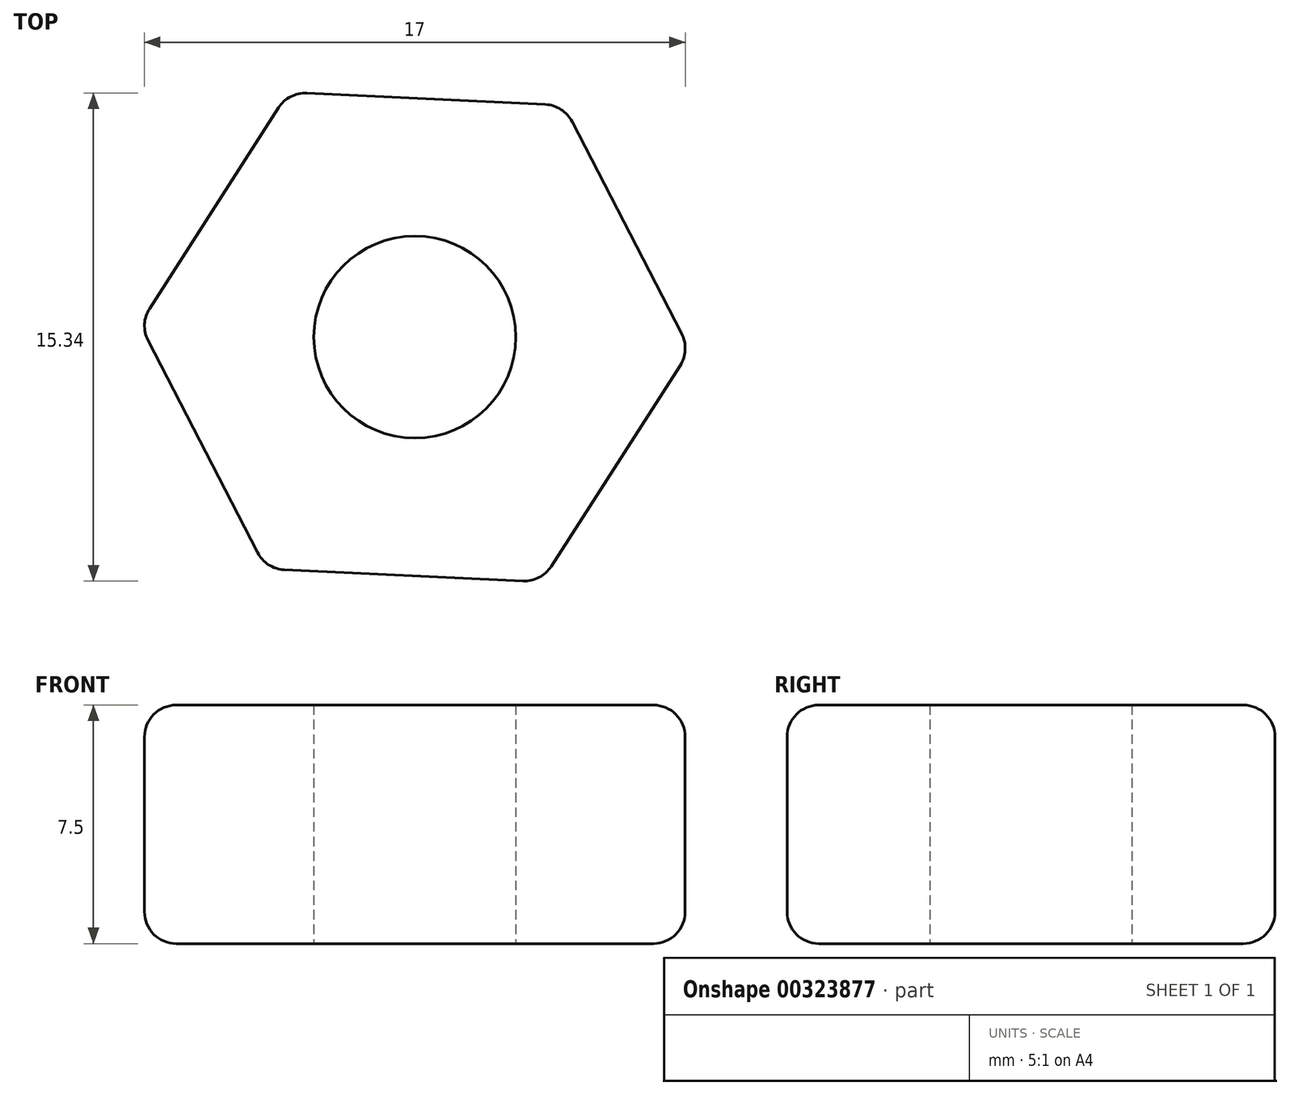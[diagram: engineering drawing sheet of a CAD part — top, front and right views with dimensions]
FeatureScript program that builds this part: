
annotation { "Feature Type Name" : "Feature", "Feature Type Description" : "" }
export const myFeature = defineFeature(function(context is Context, id is Id, definition is map)
    precondition{}
    {
        {
            var Q0;
            Q0=qCreatedBy(makeId("Top.planeOp"),FACE);
            var sketch = newSketch(context, id + "F0", { "sketchPlane" : qUnion([Q0])});
            skCircle(sketch, "E0", {"center": v(0, 0) * mm, "radius": 3.18 * mm});
            skLineSegment(sketch, "E1.0", {"start": v(8.65, -0.4) * mm, "end": v(3.97, -7.7) * mm});
            skLineSegment(sketch, "E1.1", {"start": v(3.97, -7.7) * mm, "end": v(-4.68, -7.29) * mm});
            skLineSegment(sketch, "E1.2", {"start": v(-4.68, -7.29) * mm, "end": v(-8.65, 0.4) * mm});
            skLineSegment(sketch, "E1.3", {"start": v(-8.65, 0.4) * mm, "end": v(-3.97, 7.7) * mm});
            skLineSegment(sketch, "E1.4", {"start": v(-3.97, 7.7) * mm, "end": v(4.68, 7.29) * mm});
            skLineSegment(sketch, "E1.5", {"start": v(4.68, 7.29) * mm, "end": v(8.65, -0.4) * mm});
            skPoint(sketch, "E1.0.midPoint", {"position": v(6.31, -4.05) * mm});
            skSolve(sketch);
        }
        {
            var Q0;
            Q0=makeQuery(id+"F0.imprint","IMPRINT",FACE,{"disambiguationData":[TD([[makeQuery(id+"F0.imprint","IMPRINT",EDGE,{"derivedFrom":sQuery(id+"F0.wireOp",EDGE,"E0")}),-1.0]])]});
            extrude(context, id + "F1", {"entities" : qUnion([Q0]), "depth" : 7.5 * mm});
        }
        {
            var Q0;
            Q0=makeQuery(id+"F1.opExtrude","CAP_EDGE",EDGE,{"disambiguationData":[OSD([sQuery(id+"F0.wireOp",EDGE,"E1.0")])],"isStart":false});
            var Q1;
            Q1=makeQuery(id+"F1.opExtrude","CAP_EDGE",EDGE,{"disambiguationData":[OSD([sQuery(id+"F0.wireOp",EDGE,"E1.0")])],"isStart":true});
            var Q2;
            Q2=makeQuery(id+"F1.opExtrude","CAP_EDGE",EDGE,{"disambiguationData":[OSD([sQuery(id+"F0.wireOp",EDGE,"E1.1")])],"isStart":false});
            var Q3;
            Q3=makeQuery(id+"F1.opExtrude","CAP_EDGE",EDGE,{"disambiguationData":[OSD([sQuery(id+"F0.wireOp",EDGE,"E1.2")])],"isStart":false});
            var Q4;
            Q4=makeQuery(id+"F1.opExtrude","CAP_EDGE",EDGE,{"disambiguationData":[OSD([sQuery(id+"F0.wireOp",EDGE,"E1.3")])],"isStart":false});
            var Q5;
            Q5=makeQuery(id+"F1.opExtrude","CAP_EDGE",EDGE,{"disambiguationData":[OSD([sQuery(id+"F0.wireOp",EDGE,"E1.4")])],"isStart":false});
            var Q6;
            Q6=makeQuery(id+"F1.opExtrude","CAP_EDGE",EDGE,{"disambiguationData":[OSD([sQuery(id+"F0.wireOp",EDGE,"E1.5")])],"isStart":false});
            var Q7;
            Q7=makeQuery(id+"F1.opExtrude","CAP_EDGE",EDGE,{"disambiguationData":[OSD([sQuery(id+"F0.wireOp",EDGE,"E1.1")])],"isStart":true});
            var Q8;
            Q8=makeQuery(id+"F1.opExtrude","CAP_EDGE",EDGE,{"disambiguationData":[OSD([sQuery(id+"F0.wireOp",EDGE,"E1.5")])],"isStart":true});
            var Q9;
            Q9=makeQuery(id+"F1.opExtrude","SWEPT_EDGE",EDGE,{"disambiguationData":[OSD([sQuery(id+"F0.wireOp",EDGE,"E1.0"),sQuery(id+"F0.wireOp",EDGE,"E1.1")])]});
            var Q10;
            Q10=makeQuery(id+"F1.opExtrude","SWEPT_EDGE",EDGE,{"disambiguationData":[OSD([sQuery(id+"F0.wireOp",EDGE,"E1.1"),sQuery(id+"F0.wireOp",EDGE,"E1.2")])]});
            var Q11;
            Q11=makeQuery(id+"F1.opExtrude","SWEPT_EDGE",EDGE,{"disambiguationData":[OSD([sQuery(id+"F0.wireOp",EDGE,"E1.0"),sQuery(id+"F0.wireOp",EDGE,"E1.5")])]});
            var Q12;
            Q12=makeQuery(id+"F1.opExtrude","SWEPT_EDGE",EDGE,{"disambiguationData":[OSD([sQuery(id+"F0.wireOp",EDGE,"E1.4"),sQuery(id+"F0.wireOp",EDGE,"E1.5")])]});
            var Q13;
            Q13=makeQuery(id+"F1.opExtrude","CAP_EDGE",EDGE,{"disambiguationData":[OSD([sQuery(id+"F0.wireOp",EDGE,"E1.2")])],"isStart":true});
            var Q14;
            Q14=makeQuery(id+"F1.opExtrude","SWEPT_FACE",FACE,{"disambiguationData":[OSD([sQuery(id+"F0.wireOp",EDGE,"E1.2")])]});
            var Q15;
            Q15=makeQuery(id+"F1.opExtrude","CAP_EDGE",EDGE,{"disambiguationData":[OSD([sQuery(id+"F0.wireOp",EDGE,"E1.3")])],"isStart":true});
            var Q16;
            Q16=makeQuery(id+"F1.opExtrude","SWEPT_EDGE",EDGE,{"disambiguationData":[OSD([sQuery(id+"F0.wireOp",EDGE,"E1.3"),sQuery(id+"F0.wireOp",EDGE,"E1.4")])]});
            var Q17;
            Q17=makeQuery(id+"F1.opExtrude","CAP_EDGE",EDGE,{"disambiguationData":[OSD([sQuery(id+"F0.wireOp",EDGE,"E1.4")])],"isStart":true});
            fillet(context, id + "F2", {"entities" : qUnion([Q0, Q1, Q2, Q3, Q4, Q5, Q6, Q7, Q8, Q9, Q10, Q11, Q12, Q13, Q14, Q15, Q16, Q17]), "radius" : 1 * mm, "tangentPropagation" : true, "allowEdgeOverflow" : false});
        }
    });
